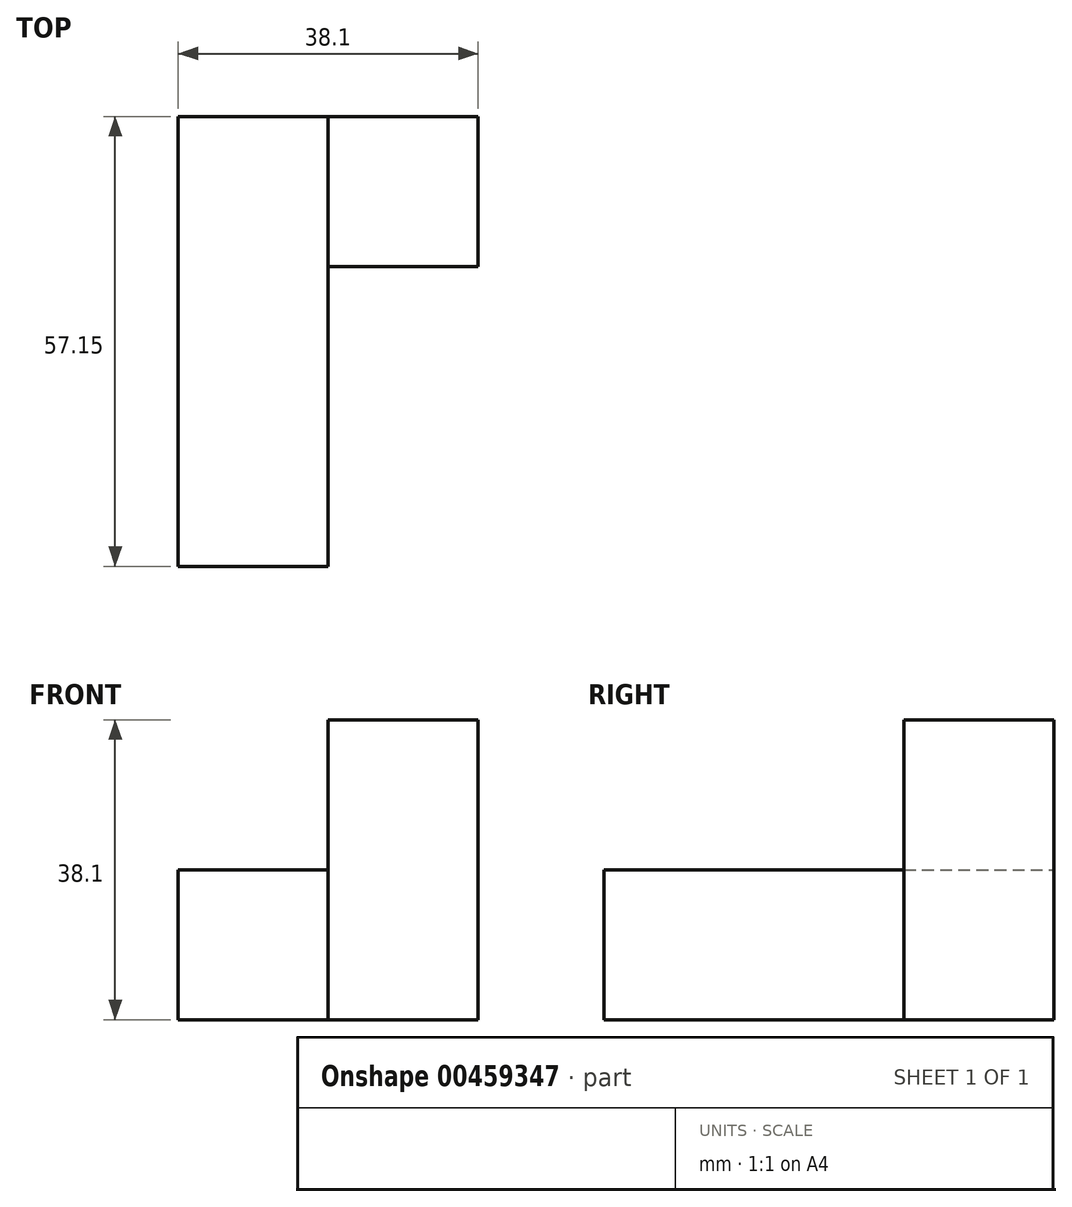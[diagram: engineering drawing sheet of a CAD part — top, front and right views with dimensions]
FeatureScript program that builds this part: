
annotation { "Feature Type Name" : "Feature", "Feature Type Description" : "" }
export const myFeature = defineFeature(function(context is Context, id is Id, definition is map)
    precondition{}
    {
        {
            var Q0;
            Q0=qCreatedBy(makeId("Top.planeOp"),FACE);
            var sketch = newSketch(context, id + "F0", { "sketchPlane" : qUnion([Q0])});
            skLineSegment(sketch, "E0", {"start": v(0, 0) * mm, "end": v(0, 19.05) * mm});
            skLineSegment(sketch, "E1", {"start": v(-19.05, 0) * mm, "end": v(-19.05, -38.1) * mm});
            skLineSegment(sketch, "E2", {"start": v(-19.05, -38.1) * mm, "end": v(0, -38.1) * mm});
            skLineSegment(sketch, "E3", {"start": v(0, -38.1) * mm, "end": v(0, 0) * mm});
            skLineSegment(sketch, "E4", {"start": v(0, 0) * mm, "end": v(19.05, 0) * mm});
            skLineSegment(sketch, "E5", {"start": v(19.05, 0) * mm, "end": v(19.05, 19.05) * mm});
            skLineSegment(sketch, "E6", {"start": v(19.05, 19.05) * mm, "end": v(0, 19.05) * mm});
            skLineSegment(sketch, "E7", {"start": v(-19.05, 0) * mm, "end": v(-19.05, 19.05) * mm});
            skLineSegment(sketch, "E8", {"start": v(-19.05, 19.05) * mm, "end": v(0, 19.05) * mm});
            skSolve(sketch);
        }
        {
            var Q0;
            {var subQ1=sQuery(id+"F0.wireOp",EDGE,"E0");Q0=makeQuery(id+"F0.imprint","IMPRINT",FACE,{"disambiguationData":[TD([[makeQuery(id+"F0.imprint","IMPRINT",EDGE,{"derivedFrom":subQ1}),1.0]])]});}
            extrude(context, id + "F1", {"entities" : qUnion([Q0]), "depth" : 19.05 * mm});
        }
        {
            var Q0;
            Q0=makeQuery(id+"F0.imprint","IMPRINT",FACE,{"disambiguationData":[TD([[makeQuery(id+"F0.imprint","IMPRINT",EDGE,{"derivedFrom":sQuery(id+"F0.wireOp",EDGE,"E0")}),-1.0]])]});
            extrude(context, id + "F2", {"entities" : qUnion([Q0]), "operationType" : NewBodyOperationType.ADD, "depth" : 38.1 * mm});
        }
    });
